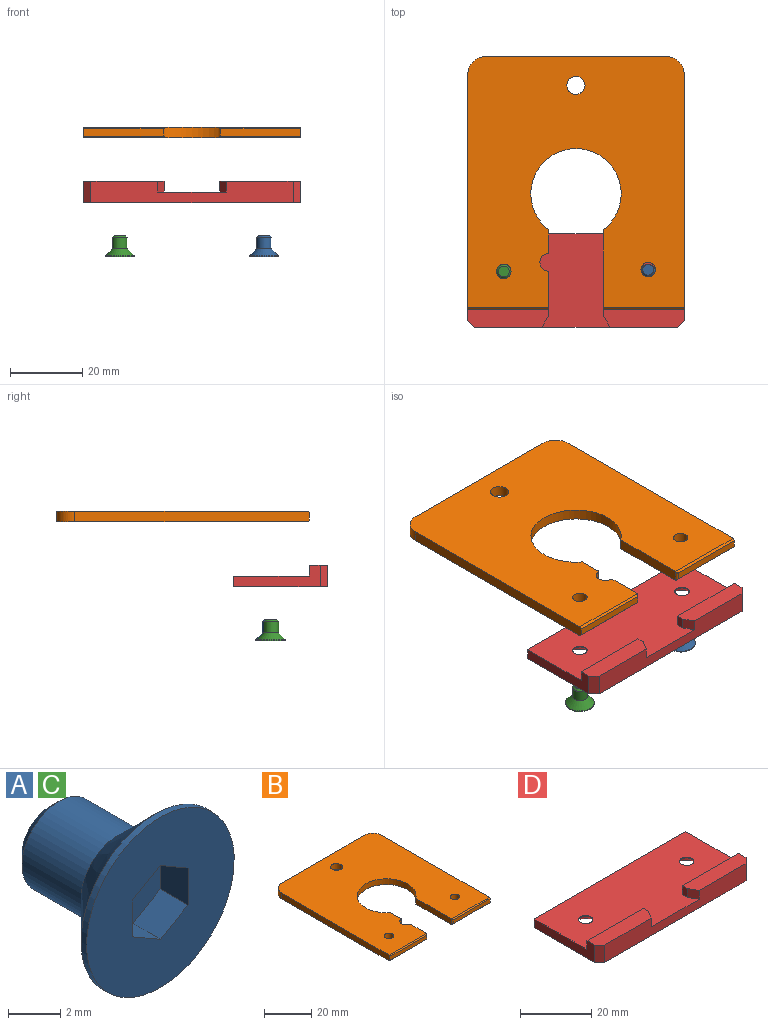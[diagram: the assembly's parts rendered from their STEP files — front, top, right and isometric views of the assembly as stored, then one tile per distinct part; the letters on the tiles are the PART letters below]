
ASSEMBLY  parts=4 mates=3
PART A: 13 faces, bbox 8x6x8 mm
  f0: plane 8x8mm, normal (0,-1,0), area 42.5mm2, adj f1,f5,f6,f7,f8,f9,f10
  f1: cylinder r=4mm len=8mm, axis (0,1,0), area 7.5mm2, adj f0,f2
  f2: cone r=2mm half-angle=45deg, axis (0,-1,0), area 53.3mm2, adj f1,f3
  f3: cylinder r=2mm len=4mm, axis (0,1,0), area 40.2mm2, adj f2,f12
  f4: plane 3x3mm, normal (0,1,0), area 7.1mm2, adj f12
  f5: plane 1.5x1.5mm, normal (0.5,0,0.87), area 2.6mm2, adj f0,f6,f10,f11
  f6: plane 1.5x1.5mm, normal (-0.5,0,0.87), area 2.6mm2, adj f0,f5,f7,f11
  f7: plane 1.73x1.5mm, normal (-1,0,0), area 2.6mm2, adj f0,f6,f8,f11
  f8: plane 1.5x1.5mm, normal (-0.5,0,-0.87), area 2.6mm2, adj f0,f7,f9,f11
  f9: plane 1.5x1.5mm, normal (0.5,0,-0.87), area 2.6mm2, adj f0,f8,f10,f11
  f10: plane 1.73x1.5mm, normal (1,0,0), area 2.6mm2, adj f0,f5,f9,f11
  f11: plane 3.46x3mm, normal (0,-1,0), area 7.8mm2, adj f5,f6,f7,f8,f9,f10
  f12: cone r=1.5mm half-angle=45deg, axis (0,-1,0), area 7.8mm2, adj f3,f4
PART B: 25 faces, bbox 60x70x3 mm
  f0: plane 22x2mm, normal (0,-1,0), area 44mm2, adj f1,f17,f20,f22
  f1: plane 65x3mm, normal (1,0,0), area 194.8mm2, adj f0,f11,f12,f13,f17,f20
  f2: plane 50x3mm, normal (0,1,0), area 150mm2, adj f11,f12,f13,f14
  f3: plane 65x3mm, normal (-1,0,0), area 194.8mm2, adj f4,f11,f12,f14,f18,f19
  f4: plane 22x2mm, normal (0,-1,0), area 44mm2, adj f3,f18,f19,f21
  f5: plane 9.54x3mm, normal (1,0,0), area 28.6mm2, adj f11,f12,f21,f23
  f6: cylinder r=2.5mm len=4.93mm, axis (0,0,-1), area 21.1mm2, adj f11,f12,f23,f24
  f7: plane 6.04x3mm, normal (1,0,0), area 18.1mm2, adj f8,f11,f12,f24
  f8: cylinder r=12.5mm len=25mm, axis (0,0,-1), area 187.4mm2, adj f7,f10,f11,f12
  f9: cylinder r=2.5mm len=5mm, axis (0,0,-1), area 47.1mm2, adj f11,f12
  f10: plane 21.5x3mm, normal (-1,0,0), area 64.5mm2, adj f8,f11,f12,f22
  f11: plane 69.5x60mm, normal (0,0,1), area 3316.8mm2, adj f1,f2,f3,f5,f6,f7,f8,f9
  f12: plane 69.5x60mm, normal (0,0,-1), area 3316.8mm2, adj f1,f2,f3,f5,f6,f7,f8,f9
  f13: cylinder r=5mm len=5mm, axis (0,0,-1), area 23.6mm2, adj f1,f2,f11,f12
  f14: cylinder r=5mm len=5mm, axis (0,0,-1), area 23.6mm2, adj f2,f3,f11,f12
  f15: cylinder r=2mm len=4mm, axis (0,0,1), area 37.7mm2, adj f11,f12
  f16: cylinder r=2mm len=4mm, axis (0,0,1), area 37.7mm2, adj f11,f12
  f17: plane 22.5x0.5mm, normal (0,-0.71,-0.71), area 15.8mm2, adj f0,f1,f12,f22
  f18: plane 22.5x0.5mm, normal (0,-0.71,-0.71), area 15.8mm2, adj f3,f4,f12,f21
  f19: plane 22.5x0.5mm, normal (0,-0.71,0.71), area 15.8mm2, adj f3,f4,f11,f21
  f20: plane 22.5x0.5mm, normal (0,-0.71,0.71), area 15.8mm2, adj f0,f1,f11,f22
  f21: cylinder r=0.5mm len=3mm, axis (0,0,-1), area 1.9mm2, adj f4,f5,f18,f19
  f22: cylinder r=0.5mm len=3mm, axis (0,0,1), area 1.9mm2, adj f0,f10,f17,f20
  f23: cylinder r=0.5mm len=3mm, axis (0,0,-1), area 2.1mm2, adj f5,f6,f11,f12
  f24: cylinder r=0.5mm len=3mm, axis (0,0,-1), area 2.1mm2, adj f6,f7,f11,f12
PART C: same geometry as A
PART D: 20 faces, bbox 60x26x6 mm
  f0: plane 22.25x5mm, normal (0,0,1), area 106.7mm2, adj f1,f2,f4,f10,f12,f18
  f1: plane 22.25x3mm, normal (0,1,0), area 66.7mm2, adj f0,f2,f9,f10
  f2: plane 24x6mm, normal (-1,0,0), area 81mm2, adj f0,f1,f3,f7,f9,f18
  f3: plane 60x3mm, normal (0,1,0), area 180mm2, adj f2,f5,f7,f9
  f4: plane 56x6mm, normal (0,-1,0), area 279.3mm2, adj f0,f6,f7,f9,f12,f13,f18,f19
  f5: plane 24x6mm, normal (1,0,0), area 81mm2, adj f3,f6,f7,f8,f9,f19
  f6: plane 22.25x5mm, normal (0,0,1), area 106.7mm2, adj f4,f5,f8,f11,f13,f19
  f7: plane 60x26mm, normal (0,0,-1), area 1414.2mm2, adj f2,f3,f4,f5,f16,f17,f18,f19
  f8: plane 22.25x3mm, normal (0,1,0), area 66.7mm2, adj f5,f6,f9,f11
  f9: plane 60x26mm, normal (0,0,1), area 1317.5mm2, adj f1,f2,f3,f4,f5,f8,f10,f11
  f10: plane 3x2mm, normal (1,0,0), area 6mm2, adj f0,f1,f9,f12
  f11: plane 3x2mm, normal (-1,0,0), area 6mm2, adj f6,f8,f9,f13
  f12: plane 3x3mm, normal (0.87,-0.49,0), area 10.3mm2, adj f0,f4,f9,f10
  f13: plane 3x3mm, normal (-0.87,-0.49,0), area 10.3mm2, adj f4,f6,f9,f11
  f14: cylinder r=2mm len=4mm, axis (0,0,1), area 3.1mm2, adj f9,f16
  f15: cylinder r=2mm len=4mm, axis (0,0,1), area 3.1mm2, adj f9,f17
  f16: cone r=4.75mm half-angle=45deg, axis (0,0,-1), area 82.5mm2, adj f7,f14
  f17: cone r=4.75mm half-angle=45deg, axis (0,0,-1), area 82.5mm2, adj f7,f15
  f18: plane 6x2mm, normal (-0.71,-0.71,0), area 17mm2, adj f0,f2,f4,f7
  f19: plane 6x2mm, normal (0.71,-0.71,0), area 17mm2, adj f4,f5,f6,f7
PLACE A rot(axis=(1,0,0),90deg) t=(53.45,2.7,-23.41)mm
PLACE B t=(3.45,-8.3,9.59)mm
PLACE C rot(axis=(1,0,0),90deg) t=(13.45,2.2,-23.41)mm
PLACE D t=(3.45,-13.3,-8.41)mm
MATE fastened A.f2 <-> B.f16  axis (0,0,1) through (53.45,2.7,-17.41)mm
MATE fastened D.f15 <-> B.f15  axis (0,0,1) through (13.45,2.2,-5.41)mm
MATE fastened C.f2 <-> B.f15  axis (0,0,1) through (13.45,2.2,-17.41)mm
